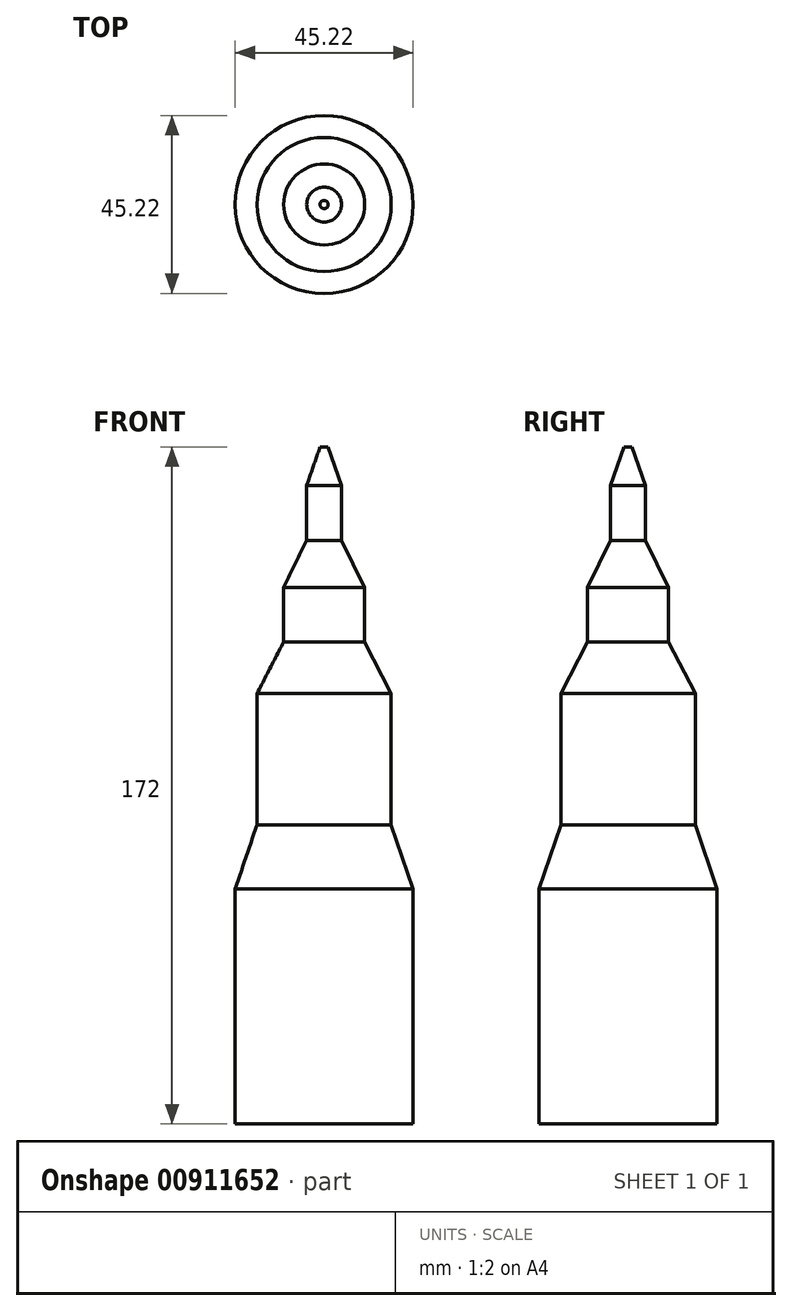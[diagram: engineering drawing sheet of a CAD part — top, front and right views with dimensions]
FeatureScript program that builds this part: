
annotation { "Feature Type Name" : "Feature", "Feature Type Description" : "" }
export const myFeature = defineFeature(function(context is Context, id is Id, definition is map)
    precondition{}
    {
        {
            var Q0;
            Q0=qCreatedBy(makeId("Front.planeOp"),FACE);
            var sketch = newSketch(context, id + "F0", { "sketchPlane" : qUnion([Q0])});
            skLineSegment(sketch, "E0.bottom", {"start": v(-22.6, -76.04) * mm, "end": v(0, -76.04) * mm});
            skLineSegment(sketch, "E0.left", {"start": v(-22.6, -76.04) * mm, "end": v(-22.6, -16.35) * mm});
            skLineSegment(sketch, "E0.right", {"start": v(0, -76.04) * mm, "end": v(0, -16.35) * mm});
            skLineSegment(sketch, "E1", {"start": v(-22.6, -16.35) * mm, "end": v(-17.05, 0) * mm});
            skLineSegment(sketch, "E2.left", {"start": v(-17.05, 0) * mm, "end": v(-17.05, 33.33) * mm});
            skLineSegment(sketch, "E2.right", {"start": v(0, 0) * mm, "end": v(0, 33.33) * mm});
            skLineSegment(sketch, "E3", {"start": v(-17.05, 33.33) * mm, "end": v(-10.3, 46.44) * mm});
            skLineSegment(sketch, "E4.left", {"start": v(-10.3, 46.44) * mm, "end": v(-10.3, 60.25) * mm});
            skLineSegment(sketch, "E4.right", {"start": v(0, 46.44) * mm, "end": v(0, 60.25) * mm});
            skLineSegment(sketch, "E5", {"start": v(-10.3, 60.25) * mm, "end": v(-4.43, 72.24) * mm});
            skLineSegment(sketch, "E6.left", {"start": v(-4.43, 72.24) * mm, "end": v(-4.43, 86.18) * mm});
            skLineSegment(sketch, "E6.right", {"start": v(0, 72.24) * mm, "end": v(0, 86.18) * mm});
            skLineSegment(sketch, "E7", {"start": v(-4.43, 86.18) * mm, "end": v(-1.04, 95.96) * mm});
            skLineSegment(sketch, "E8", {"start": v(-1.04, 95.96) * mm, "end": v(0, 95.96) * mm});
            skLineSegment(sketch, "E9", {"start": v(0, 95.96) * mm, "end": v(0, -82.76) * mm});
            skLineSegment(sketch, "E10", {"start": v(0, -82.76) * mm, "end": v(0, 99.89) * mm});
            skSolve(sketch);
        }
        {
            var Q0;
            Q0 = qSketchRegion(id + "F0", true);
            var Q1;
            Q1=sQuery(id+"F0.wireOp",EDGE,"E10");
            revolve(context, id + "F1", {"surfaceOperationType" : NewSurfaceOperationType.NEW, "entities" : qUnion([Q0]), "axis" : qUnion([Q1]), "revolveType" : RevolveType.FULL});
        }
    });
